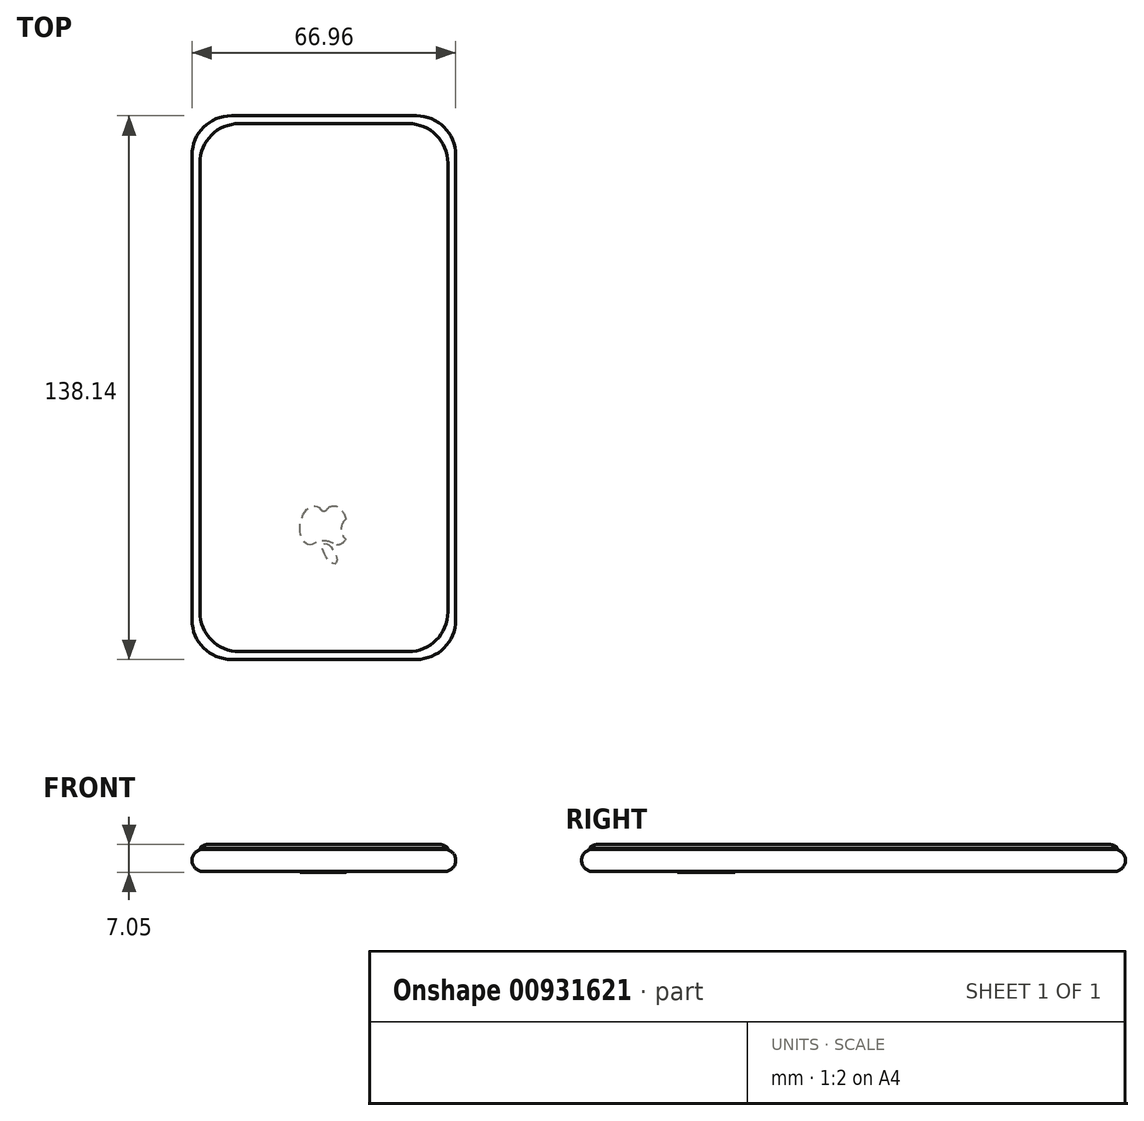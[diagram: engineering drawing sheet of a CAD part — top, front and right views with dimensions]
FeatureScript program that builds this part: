
annotation { "Feature Type Name" : "Feature", "Feature Type Description" : "" }
export const myFeature = defineFeature(function(context is Context, id is Id, definition is map)
    precondition{}
    {
        {
            assignVariable(context, id + "F0", {"name" : "GlassThick", "anyValue" : .96});
        }
        {
            assignVariable(context, id + "F1", {"name" : "HousingThick", "anyValue" : 6.55 - getVariable(context, 'GlassThick')});
        }
        {
            assignVariable(context, id + "F2", {"name" : "BlackBody", "anyValue" : .3});
        }
        {
            var Q0;
            Q0=qCreatedBy(makeId("Top.planeOp"),FACE);
            var sketch = newSketch(context, id + "F3", { "sketchPlane" : qUnion([Q0])});
            skLineSegment(sketch, "E0.bottom", {"start": v(33.49, 69.07) * mm, "end": v(-33.48, 69.07) * mm});
            skLineSegment(sketch, "E0.top", {"start": v(33.48, -69.07) * mm, "end": v(-33.49, -69.07) * mm});
            skLineSegment(sketch, "E0.left", {"start": v(33.49, 69.07) * mm, "end": v(33.48, -69.07) * mm});
            skLineSegment(sketch, "E0.right", {"start": v(-33.48, 69.07) * mm, "end": v(-33.48, -69.07) * mm});
            skPoint(sketch, "E0.middle", {"position": v(0, 0) * mm});
            skSolve(sketch);
        }
        {
            var Q0;
            Q0=makeQuery(id+"F3.imprint","IMPRINT",FACE,{"disambiguationData":[TD([[makeQuery(id+"F3.imprint","IMPRINT",EDGE,{"derivedFrom":sQuery(id+"F3.wireOp",EDGE,"E0.bottom")}),1.0]])]});
            extrude(context, id + "F4", {"entities" : qUnion([Q0]), "depth" : (getVariable(context, 'HousingThick')) * mm, "offsetDistance" : 25 * mm});
        }
        {
            var Q0;
            Q0=makeQuery(id+"F4.opExtrude","CAP_FACE",FACE,{"disambiguationData":[OSD([sQuery(id+"F3.wireOp",EDGE,"E0.bottom"),sQuery(id+"F3.wireOp",EDGE,"E0.top"),sQuery(id+"F3.wireOp",EDGE,"E0.left"),sQuery(id+"F3.wireOp",EDGE,"E0.right")])],"isStart":false});
            var sketch = newSketch(context, id + "F5", { "sketchPlane" : qUnion([Q0])});
            skLineSegment(sketch, "E1.bottom", {"start": v(33.49, 69.07) * mm, "end": v(-33.49, 69.07) * mm, "construction": true});
            skLineSegment(sketch, "E1.top", {"start": v(33.49, -69.07) * mm, "end": v(-33.49, -69.07) * mm, "construction": true});
            skLineSegment(sketch, "E1.left", {"start": v(33.49, 69.07) * mm, "end": v(33.49, -69.07) * mm, "construction": true});
            skLineSegment(sketch, "E1.right", {"start": v(-33.49, 69.07) * mm, "end": v(-33.49, -69.07) * mm, "construction": true});
            skPoint(sketch, "E1.middle", {"position": v(0, 0) * mm});
            skLineSegment(sketch, "E2.0", {"start": v(31.49, 67.07) * mm, "end": v(-31.49, 67.07) * mm});
            skLineSegment(sketch, "E2.1", {"start": v(31.49, 67.07) * mm, "end": v(31.49, -67.07) * mm});
            skLineSegment(sketch, "E2.2", {"start": v(31.49, -67.07) * mm, "end": v(-31.49, -67.07) * mm});
            skLineSegment(sketch, "E2.3", {"start": v(-31.49, 67.07) * mm, "end": v(-31.49, -67.07) * mm});
            skSolve(sketch);
        }
        {
            var Q0;
            Q0 = qSketchRegion(id + "F5", true);
            extrude(context, id + "F6", {"entities" : qUnion([Q0]), "depth" : (getVariable(context, 'BlackBody')) * mm, "offsetDistance" : 25 * mm});
        }
        {
            var Q0;
            Q0=makeQuery(id+"F6.opExtrude","CAP_FACE",FACE,{"disambiguationData":[OSD([sQuery(id+"F5.wireOp",EDGE,"E2.0"),sQuery(id+"F5.wireOp",EDGE,"E2.1"),sQuery(id+"F5.wireOp",EDGE,"E2.2"),sQuery(id+"F5.wireOp",EDGE,"E2.3")])],"isStart":false});
            var sketch = newSketch(context, id + "F7", { "sketchPlane" : qUnion([Q0])});
            skLineSegment(sketch, "E3.bottom", {"start": v(31.49, 67.07) * mm, "end": v(-31.49, 67.07) * mm});
            skLineSegment(sketch, "E3.top", {"start": v(31.49, -67.07) * mm, "end": v(-31.49, -67.07) * mm});
            skLineSegment(sketch, "E3.left", {"start": v(31.49, 67.07) * mm, "end": v(31.49, -67.07) * mm});
            skLineSegment(sketch, "E3.right", {"start": v(-31.49, 67.07) * mm, "end": v(-31.49, -67.07) * mm});
            skPoint(sketch, "E3.middle", {"position": v(0, 0) * mm});
            skSolve(sketch);
        }
        {
            var Q0;
            Q0 = qSketchRegion(id + "F7", true);
            extrude(context, id + "F8", {"entities" : qUnion([Q0]), "depth" : (getVariable(context, 'GlassThick')) * mm, "offsetDistance" : 25 * mm});
        }
        {
            var Q0;
            Q0=makeQuery(id+"F4.opExtrude","SWEPT_EDGE",EDGE,{"disambiguationData":[OSD([sQuery(id+"F3.wireOp",EDGE,"E0.bottom"),sQuery(id+"F3.wireOp",EDGE,"E0.right")])]});
            var Q1;
            Q1=makeQuery(id+"F6.opExtrude","SWEPT_EDGE",EDGE,{"disambiguationData":[OSD([sQuery(id+"F5.wireOp",EDGE,"I0zcJkxY-vnls-8RsF-3nQE-bTOEe2NIqflo.bottom"),sQuery(id+"F5.wireOp",EDGE,"I0zcJkxY-vnls-8RsF-3nQE-bTOEe2NIqflo.right")])]});
            var Q2;
            Q2=makeQuery(id+"F8.opExtrude","SWEPT_EDGE",EDGE,{"disambiguationData":[OSD([sQuery(id+"F7.wireOp",EDGE,"E3.bottom"),sQuery(id+"F7.wireOp",EDGE,"E3.right")])]});
            var Q3;
            Q3=makeQuery(id+"F8.opExtrude","SWEPT_EDGE",EDGE,{"disambiguationData":[OSD([sQuery(id+"F7.wireOp",EDGE,"E3.top"),sQuery(id+"F7.wireOp",EDGE,"E3.right")])]});
            var Q4;
            Q4=makeQuery(id+"F6.opExtrude","SWEPT_EDGE",EDGE,{"disambiguationData":[OSD([sQuery(id+"F5.wireOp",EDGE,"I0zcJkxY-vnls-8RsF-3nQE-bTOEe2NIqflo.top"),sQuery(id+"F5.wireOp",EDGE,"I0zcJkxY-vnls-8RsF-3nQE-bTOEe2NIqflo.right")])]});
            var Q5;
            Q5=makeQuery(id+"F4.opExtrude","SWEPT_EDGE",EDGE,{"disambiguationData":[OSD([sQuery(id+"F3.wireOp",EDGE,"E0.top"),sQuery(id+"F3.wireOp",EDGE,"E0.right")])]});
            var Q6;
            Q6=makeQuery(id+"F6.opExtrude","SWEPT_EDGE",EDGE,{"disambiguationData":[OSD([sQuery(id+"F5.wireOp",EDGE,"I0zcJkxY-vnls-8RsF-3nQE-bTOEe2NIqflo.top"),sQuery(id+"F5.wireOp",EDGE,"I0zcJkxY-vnls-8RsF-3nQE-bTOEe2NIqflo.left")])]});
            var Q7;
            Q7=makeQuery(id+"F8.opExtrude","SWEPT_EDGE",EDGE,{"disambiguationData":[OSD([sQuery(id+"F7.wireOp",EDGE,"E3.top"),sQuery(id+"F7.wireOp",EDGE,"E3.left")])]});
            var Q8;
            Q8=makeQuery(id+"F4.opExtrude","SWEPT_EDGE",EDGE,{"disambiguationData":[OSD([sQuery(id+"F3.wireOp",EDGE,"E0.top"),sQuery(id+"F3.wireOp",EDGE,"E0.left")])]});
            var Q9;
            Q9=makeQuery(id+"F6.opExtrude","SWEPT_EDGE",EDGE,{"disambiguationData":[OSD([sQuery(id+"F5.wireOp",EDGE,"I0zcJkxY-vnls-8RsF-3nQE-bTOEe2NIqflo.bottom"),sQuery(id+"F5.wireOp",EDGE,"I0zcJkxY-vnls-8RsF-3nQE-bTOEe2NIqflo.left")])]});
            var Q10;
            Q10=makeQuery(id+"F8.opExtrude","SWEPT_EDGE",EDGE,{"disambiguationData":[OSD([sQuery(id+"F7.wireOp",EDGE,"E3.bottom"),sQuery(id+"F7.wireOp",EDGE,"E3.left")])]});
            var Q11;
            Q11=makeQuery(id+"F4.opExtrude","SWEPT_EDGE",EDGE,{"disambiguationData":[OSD([sQuery(id+"F3.wireOp",EDGE,"E0.bottom"),sQuery(id+"F3.wireOp",EDGE,"E0.left")])]});
            var Q12;
            Q12=makeQuery(id+"F6.opExtrude","SWEPT_EDGE",EDGE,{"disambiguationData":[OSD([sQuery(id+"F5.wireOp",EDGE,"E2.0"),sQuery(id+"F5.wireOp",EDGE,"E2.3")])]});
            var Q13;
            Q13=makeQuery(id+"F6.opExtrude","SWEPT_EDGE",EDGE,{"disambiguationData":[OSD([sQuery(id+"F5.wireOp",EDGE,"E2.0"),sQuery(id+"F5.wireOp",EDGE,"E2.1")])]});
            var Q14;
            Q14=makeQuery(id+"F6.opExtrude","SWEPT_EDGE",EDGE,{"disambiguationData":[OSD([sQuery(id+"F5.wireOp",EDGE,"E2.1"),sQuery(id+"F5.wireOp",EDGE,"E2.2")])]});
            var Q15;
            Q15=makeQuery(id+"F6.opExtrude","SWEPT_EDGE",EDGE,{"disambiguationData":[OSD([sQuery(id+"F5.wireOp",EDGE,"E2.2"),sQuery(id+"F5.wireOp",EDGE,"E2.3")])]});
            fillet(context, id + "F9", {"entities" : qUnion([Q0, Q1, Q2, Q3, Q4, Q5, Q6, Q7, Q8, Q9, Q10, Q11, Q12, Q13, Q14, Q15]), "radius" : 10 * mm, "tangentPropagation" : true, "allowEdgeOverflow" : false});
        }
        {
            var Q0;
            Q0=makeQuery(id+"F4.opExtrude","CAP_FACE",FACE,{"disambiguationData":[OSD([sQuery(id+"F3.wireOp",EDGE,"E0.bottom"),sQuery(id+"F3.wireOp",EDGE,"E0.top"),sQuery(id+"F3.wireOp",EDGE,"E0.left"),sQuery(id+"F3.wireOp",EDGE,"E0.right")])],"isStart":false});
            var Q1;
            Q1=makeQuery(id+"F4.opExtrude","CAP_FACE",FACE,{"disambiguationData":[OSD([sQuery(id+"F3.wireOp",EDGE,"E0.bottom"),sQuery(id+"F3.wireOp",EDGE,"E0.top"),sQuery(id+"F3.wireOp",EDGE,"E0.left"),sQuery(id+"F3.wireOp",EDGE,"E0.right")])],"isStart":true});
            fillet(context, id + "F10", {"entities" : qUnion([Q0, Q1]), "radius" : 2.75 * mm, "tangentPropagation" : true, "allowEdgeOverflow" : false});
        }
        {
            var Q0;
            Q0=makeQuery(id+"F8.opExtrude","CAP_FACE",FACE,{"disambiguationData":[OSD([sQuery(id+"F7.wireOp",EDGE,"E3.bottom"),sQuery(id+"F7.wireOp",EDGE,"E3.top"),sQuery(id+"F7.wireOp",EDGE,"E3.left"),sQuery(id+"F7.wireOp",EDGE,"E3.right")])],"isStart":false});
            fillet(context, id + "F11", {"entities" : qUnion([Q0]), "radius" : 2.75 * mm, "tangentPropagation" : true, "allowEdgeOverflow" : false});
        }
        {
            var Q0;
            Q0=makeQuery(id+"F4.opExtrude","CAP_FACE",FACE,{"disambiguationData":[OSD([sQuery(id+"F3.wireOp",EDGE,"E0.bottom"),sQuery(id+"F3.wireOp",EDGE,"E0.top"),sQuery(id+"F3.wireOp",EDGE,"E0.left"),sQuery(id+"F3.wireOp",EDGE,"E0.right")])],"isStart":true});
            var sketch = newSketch(context, id + "F12", { "sketchPlane" : qUnion([Q0])});
            skEllipticalArc(sketch, "E4", {});
            skLineSegment(sketch, "E5", {"start": v(0, 24.15) * mm, "end": v(-7.94, 24.15) * mm, "construction": true});
            skLineSegment(sketch, "E6", {"start": v(-3.87, 39.92) * mm, "end": v(-3.87, 39.92) * mm});
            skLineSegment(sketch, "E7", {"start": v(-3.87, 39.92) * mm, "end": v(-2.13, 30.08) * mm, "construction": true});
            skPoint(sketch, "E7.endSnap0", {"position": v(-2.13, 30.08) * mm});
            skLineSegment(sketch, "E8", {"start": v(0, 44.1) * mm, "end": v(0, 24.15) * mm, "construction": true});
            skEllipticalArc(sketch, "E9.MirrorC", {});
            skPoint(sketch, "E10.visualSharp", {"position": v(0, 35.23) * mm});
            skArc(sketch, "E10.filletArc", {"start": v(-2.47, 39.64) * mm, "mid": v(0, 39) * mm, "end": v(2.47, 39.64) * mm});
            skPoint(sketch, "E11.visualSharp", {"position": v(0, 33.04) * mm});
            skArc(sketch, "E11.filletArc", {"start": v(0.8, 30.96) * mm, "mid": v(0, 31.36) * mm, "end": v(-0.8, 30.96) * mm});
            skEllipse(sketch, "E12", {"center": v(1.5, 42.2) * mm, "majorRadius": 2.88 * mm, "minorRadius": 1.25 * mm, "majorAxis": v(-0.5, -0.87)});
            skLineSegment(sketch, "E13", {"start": v(2.94, 44.69) * mm, "end": v(0.06, 39.71) * mm, "construction": true});
            skArc(sketch, "E14", {"start": v(5.56, 38.45) * mm, "mid": v(4.38, 35.91) * mm, "end": v(5.7, 33.44) * mm});
            skEllipticalArc(sketch, "E15.trimOffspring", {});
            const initialGuessF12  = {"E4": [-0.003, 0.035, 0.17364817766693041, -0.9848077530122081, 0.005, 0.003, 2.6815204055388673, 0.5104934757589162], "E9.MirrorC": [0.003, 0.035, -0.17364817766693022, -0.9848077530122082, 0.005, 0.003, 5.772691831420671, 1.3565160158556264], "E15.trimOffspring": [0.003, 0.035, -0.17364817766693022, -0.9848077530122082, 0.005, 0.003, 2.4467252969667457, 3.601664901640688]};
            skSetInitialGuess(sketch, initialGuessF12);
            skSolve(sketch);
        }
        {
            var Q0;
            Q0 = qSketchRegion(id + "F12", true);
            extrude(context, id + "F13", {"entities" : qUnion([Q0]), "depth" : .2 * mm, "offsetDistance" : 25 * mm});
        }
    });
